# Revit family: Pivoting wallmount cabinets Legrand Linkeo with removable side panels
name_source: partatom
category: Equipement spécialisé
units: mm (PartAtom-declared; Revit-internal decimal feet)

## family parameters
Basée sur le plan de construction = Non
Cote de connecteur circulaire = Utiliser le diamètre
Couper avec des vides une fois chargée = Non
Numéro OmniClass = 23.80.30.11.17
Partagée = Oui
Point de calcul de pièce = Non
Titre OmniClass = Distribution Boards and Control Panels
Toujours verticalement = Oui
Type d'élément = Normal

## types (5) — shared parameters
Application class = Network cabinets
Avec porte frontale = Oui
Color = grey
Degree of protection IK = IK08
Degree of protection IP = IP20
Demountable = Oui
Depth (mm) = 615 mm  [stored 2.01772 ft]
Depth of the model (mm) = 458 mm
E-catalogue link = https://www.legrand.fr
Fabricant = Legrand
Function = Pivoting wallmount cabinets Legrand Linkeo
Material = Steel
Model = With swing frame
Modular spacing = 482.6 mm (19 inches)
Mounting level = Front side
Number of doors = 1
RAL Number = 7016
Rack location = 40 mm  [stored 0.131234 ft]
Thickness (mm) = 1.5 mm  [stored 0.00492126 ft]
Type of profile rail = L-shaped
Type of surface = Powder coating
Type of ventilation = Passive
Usable width (mm) = 527 mm  [stored 1.729 ft]
Width (mm) = 642 mm  [stored 2.1063 ft]
With earthing = Oui
With roof plate = Oui
With sidewall = Oui
zero-valued in all types: Elévation par défaut

## per-type parameters (varying)
| type | Capacity | EAN | Height (mm) | Legrand part number | Max load capacity | Number of height units | Usable height (mm) |
| Pivoting wallmount cabinet Legrand Linkeo 9U W600 D610 646221.rfa | 9 | 3414970967893 | 492 mm  [stored 1.61417 ft] | 646221 | 27 | 9 | 422 mm  [stored 1.38451 ft] |
| Pivoting wallmount cabinet Legrand Linkeo 12U W600 D610 646222.rfa | 12 | 3414970967909 | 625 mm  [stored 2.05052 ft] | 646222 | 36 | 12 | 555 mm  [stored 1.82087 ft] |
| Pivoting wallmount cabinet Legrand Linkeo 15U W600 D610 646223.rfa | 15 | 3414970967916 | 759 mm  [stored 2.49016 ft] | 646223 | 45 | 15 | 688 mm  [stored 2.25722 ft] |
| Pivoting wallmount cabinet Legrand Linkeo 18U W600 D610 646224.rfa | 18 | 3414970967923 | 892 mm  [stored 2.92651 ft] | 646224 | 54 | 18 | 821 mm  [stored 2.69357 ft] |
| Pivoting wallmount cabinet Legrand Linkeo 21U W600 D610 646225.rfa | 21 | 3414970967930 | 1025 mm  [stored 3.36286 ft] | 646225 | 63 | 21 | 955 mm  [stored 3.1332 ft] |

note: column(s) folded — value = type name in every type: BIM wording

note: [stored X ft] marks values corroborated as IEEE doubles in the binary element streams (Revit-internal decimal feet)
